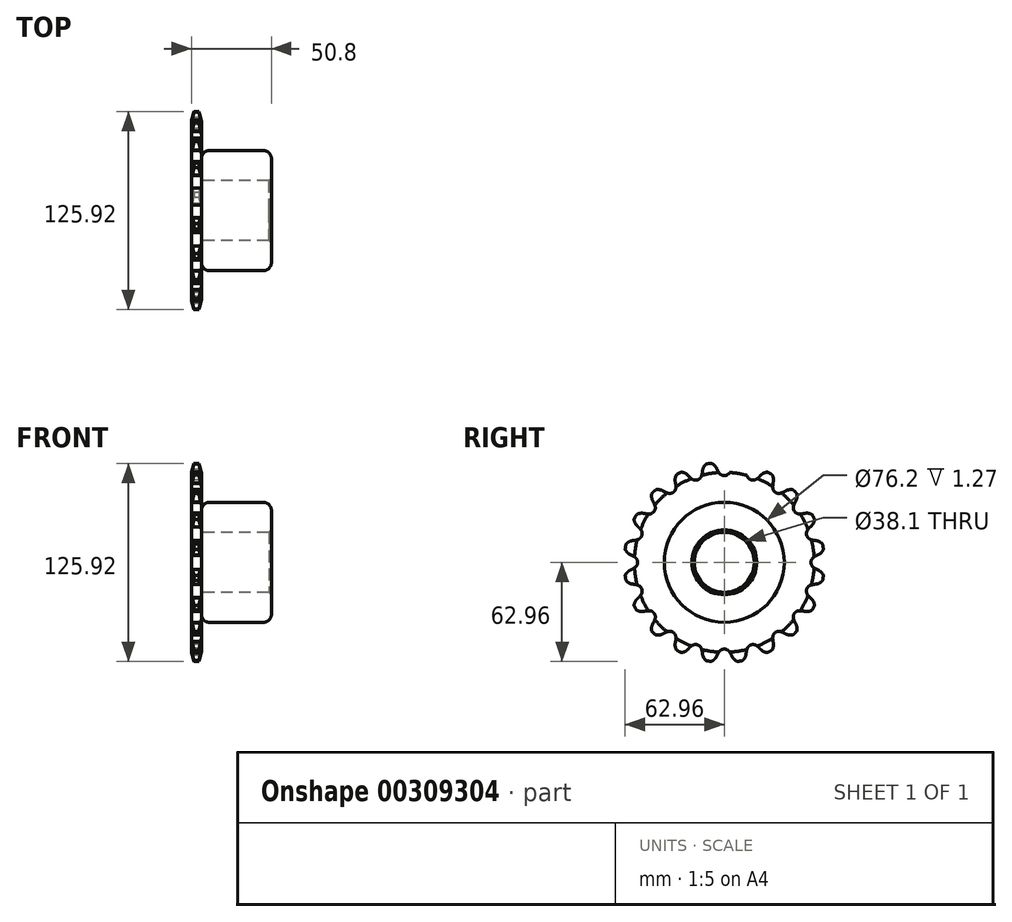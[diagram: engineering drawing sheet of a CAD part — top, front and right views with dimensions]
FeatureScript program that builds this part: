
annotation { "Feature Type Name" : "Feature", "Feature Type Description" : "" }
export const myFeature = defineFeature(function(context is Context, id is Id, definition is map)
    precondition{}
    {
        {
            var Q0;
            Q0=qCreatedBy(makeId("Top.planeOp"),FACE);
            var sketch = newSketch(context, id + "F0", { "sketchPlane" : qUnion([Q0])});
            skLineSegment(sketch, "E0", {"start": v(0, 0) * mm, "end": v(76.2, 0) * mm, "construction": true});
            skLineSegment(sketch, "E1.bottom", {"start": v(0, 19.05) * mm, "end": v(6.35, 19.05) * mm});
            skLineSegment(sketch, "E1.top", {"start": v(0, 63.5) * mm, "end": v(6.35, 63.5) * mm});
            skLineSegment(sketch, "E1.left", {"start": v(0, 19.05) * mm, "end": v(0, 63.5) * mm});
            skLineSegment(sketch, "E1.right", {"start": v(6.35, 19.05) * mm, "end": v(6.35, 63.5) * mm});
            skLineSegment(sketch, "E2.bottom", {"start": v(0, 19.05) * mm, "end": v(50.8, 19.05) * mm});
            skLineSegment(sketch, "E2.top", {"start": v(0, 38.1) * mm, "end": v(50.8, 38.1) * mm});
            skLineSegment(sketch, "E2.left", {"start": v(0, 19.05) * mm, "end": v(0, 38.1) * mm});
            skLineSegment(sketch, "E2.right", {"start": v(50.8, 19.05) * mm, "end": v(50.8, 38.1) * mm});
            skLineSegment(sketch, "E3.MirrorCS", {"start": v(0, -19.05) * mm, "end": v(6.35, -19.05) * mm});
            skLineSegment(sketch, "E4.MirrorCS", {"start": v(50.8, -19.05) * mm, "end": v(50.8, -38.1) * mm});
            skLineSegment(sketch, "E5.MirrorCS", {"start": v(0, -19.05) * mm, "end": v(0, -38.1) * mm});
            skLineSegment(sketch, "E6.MirrorCS", {"start": v(0, -19.05) * mm, "end": v(50.8, -19.05) * mm});
            skLineSegment(sketch, "E7.MirrorCS", {"start": v(0, -19.05) * mm, "end": v(0, -63.5) * mm});
            skLineSegment(sketch, "E8.MirrorCS", {"start": v(0, -38.1) * mm, "end": v(50.8, -38.1) * mm});
            skLineSegment(sketch, "E9.MirrorCS", {"start": v(0, -63.5) * mm, "end": v(6.35, -63.5) * mm});
            skLineSegment(sketch, "E10.MirrorCS", {"start": v(6.35, -19.05) * mm, "end": v(6.35, -63.5) * mm});
            skSolve(sketch);
        }
        {
            var Q0;
            {var subQ5=sQuery(id+"F0.wireOp",EDGE,"E2.right");Q0=makeQuery(id+"F0.imprint","IMPRINT",FACE,{"disambiguationData":[TD([[makeQuery(id+"F0.imprint","IMPRINT",EDGE,{"derivedFrom":subQ5}),1.0]])]});}
            var Q1;
            {var subQ5=sQuery(id+"F0.wireOp",EDGE,"E2.left");Q1=makeQuery(id+"F0.imprint","IMPRINT",FACE,{"disambiguationData":[TD([[makeQuery(id+"F0.imprint","IMPRINT",EDGE,{"derivedFrom":subQ5}),-1.0]])]});}
            var Q2;
            {var subQ0=sQuery(id+"F0.wireOp",EDGE,"E1.top");Q2=makeQuery(id+"F0.imprint","IMPRINT",FACE,{"disambiguationData":[TD([[makeQuery(id+"F0.imprint","IMPRINT",EDGE,{"derivedFrom":subQ0}),-1.0]])]});}
            var Q3;
            Q3=sQuery(id+"F0.wireOp",EDGE,"E0");
            revolve(context, id + "F1", {"entities" : qUnion([Q0, Q1, Q2]), "axis" : qUnion([Q3]), "revolveType" : RevolveType.FULL});
        }
        {
            var Q0;
            Q0=qCreatedBy(makeId("Right.planeOp"),FACE);
            var sketch = newSketch(context, id + "F2", { "sketchPlane" : qUnion([Q0])});
            skLineSegment(sketch, "E11", {"start": v(0, 0) * mm, "end": v(0, 59.03) * mm, "construction": true});
            skLineSegment(sketch, "E12", {"start": v(0, 59.03) * mm, "end": v(67.38, 59.03) * mm, "construction": true});
            skLineSegment(sketch, "E13", {"start": v(0, 59.03) * mm, "end": v(5, 63.04) * mm, "construction": true});
            skLineSegment(sketch, "E14", {"start": v(5, 63.04) * mm, "end": v(-4.46, 58.78) * mm, "construction": true});
            skLineSegment(sketch, "E15", {"start": v(-4.46, 58.78) * mm, "end": v(-7, 64.42) * mm, "construction": true});
            skLineSegment(sketch, "E16", {"start": v(0, 0) * mm, "end": v(-10.04, 63.42) * mm, "construction": true});
            skLineSegment(sketch, "E17", {"start": v(-10.04, 63.42) * mm, "end": v(-10.04, 63.42) * mm});
            skArc(sketch, "E18", {"start": v(-4.6, 59.03) * mm, "mid": v(-6.7, 62) * mm, "end": v(-10.04, 63.42) * mm});
            skArc(sketch, "E19", {"start": v(-10.04, 63.42) * mm, "mid": v(-14.96, 51.74) * mm, "end": v(-4.6, 59.03) * mm, "construction": true});
            skArc(sketch, "E20", {"start": v(-4.46, 58.78) * mm, "mid": v(-3.84, 57.62) * mm, "end": v(-3.1, 56.55) * mm});
            skArc(sketch, "E21", {"start": v(-3.1, 56.55) * mm, "mid": v(13.83, 68.45) * mm, "end": v(-4.46, 58.78) * mm, "construction": true});
            skLineSegment(sketch, "E22", {"start": v(-4.46, 58.78) * mm, "end": v(-4.46, 58.78) * mm});
            skArc(sketch, "E23", {"start": v(-3.1, 56.55) * mm, "mid": v(-1.71, 55.46) * mm, "end": v(0, 55.07) * mm});
            skLineSegment(sketch, "E24.MirrorCS", {"start": v(3.1, 56.55) * mm, "end": v(3.1, 56.55) * mm});
            skArc(sketch, "E25.MirrorCS", {"start": v(4.46, 58.78) * mm, "mid": v(3.84, 57.62) * mm, "end": v(3.1, 56.55) * mm});
            skArc(sketch, "E26.MirrorCS", {"start": v(4.6, 59.03) * mm, "mid": v(6.7, 62) * mm, "end": v(10.04, 63.42) * mm});
            skCircle(sketch, "E27", {"center": v(0, 0) * mm, "radius": 57.15 * mm});
            skLineSegment(sketch, "E28", {"start": v(4.6, 59.03) * mm, "end": v(4.46, 58.78) * mm});
            skLineSegment(sketch, "E29", {"start": v(-4.46, 58.78) * mm, "end": v(-4.6, 59.03) * mm});
            skLineSegment(sketch, "E30", {"start": v(0, 55.07) * mm, "end": v(0, 55.07) * mm});
            skArc(sketch, "E31", {"start": v(3.1, 56.55) * mm, "mid": v(1.71, 55.46) * mm, "end": v(0, 55.07) * mm});
            skArc(sketch, "E32.1.0", {"start": v(-14.54, 54.74) * mm, "mid": v(-15.5, 53.27) * mm, "end": v(-17.02, 52.37) * mm});
            skArc(sketch, "E32.1.1", {"start": v(-13.93, 57.28) * mm, "mid": v(-14.15, 55.99) * mm, "end": v(-14.54, 54.74) * mm});
            skLineSegment(sketch, "E32.1.2", {"start": v(-13.87, 57.56) * mm, "end": v(-13.93, 57.28) * mm});
            skArc(sketch, "E32.1.3", {"start": v(-13.87, 57.56) * mm, "mid": v(-12.8, 61.04) * mm, "end": v(-10.04, 63.42) * mm});
            skArc(sketch, "E32.1.4", {"start": v(-20.41, 52.83) * mm, "mid": v(-18.77, 52.21) * mm, "end": v(-17.02, 52.37) * mm});
            skArc(sketch, "E32.1.5", {"start": v(-22.4, 54.53) * mm, "mid": v(-21.46, 53.61) * mm, "end": v(-20.41, 52.83) * mm});
            skArc(sketch, "E32.1.6", {"start": v(-22.61, 54.72) * mm, "mid": v(-25.52, 56.9) * mm, "end": v(-29.15, 57.2) * mm});
            skLineSegment(sketch, "E32.1.7", {"start": v(-22.4, 54.53) * mm, "end": v(-22.61, 54.72) * mm});
            skArc(sketch, "E32.2.0", {"start": v(-30.74, 47.57) * mm, "mid": v(-31.21, 45.87) * mm, "end": v(-32.37, 44.55) * mm});
            skArc(sketch, "E32.2.1", {"start": v(-30.94, 50.17) * mm, "mid": v(-30.76, 48.88) * mm, "end": v(-30.74, 47.57) * mm});
            skLineSegment(sketch, "E32.2.2", {"start": v(-30.98, 50.46) * mm, "end": v(-30.94, 50.17) * mm});
            skArc(sketch, "E32.2.3", {"start": v(-30.98, 50.46) * mm, "mid": v(-31.03, 54.1) * mm, "end": v(-29.15, 57.2) * mm});
            skArc(sketch, "E32.2.4", {"start": v(-35.74, 43.93) * mm, "mid": v(-33.98, 43.86) * mm, "end": v(-32.37, 44.55) * mm});
            skArc(sketch, "E32.2.5", {"start": v(-38.16, 44.93) * mm, "mid": v(-36.98, 44.36) * mm, "end": v(-35.74, 43.93) * mm});
            skArc(sketch, "E32.2.6", {"start": v(-38.41, 45.05) * mm, "mid": v(-41.86, 46.23) * mm, "end": v(-45.4, 45.4) * mm});
            skLineSegment(sketch, "E32.2.7", {"start": v(-38.16, 44.93) * mm, "end": v(-38.41, 45.05) * mm});
            skArc(sketch, "E33.3.3.0", {"start": v(-43.93, 35.74) * mm, "mid": v(-43.86, 33.98) * mm, "end": v(-44.55, 32.37) * mm});
            skArc(sketch, "E33.4.3.0", {"start": v(-44.93, 38.16) * mm, "mid": v(-44.36, 36.98) * mm, "end": v(-43.93, 35.74) * mm});
            skLineSegment(sketch, "E33.8.3.0", {"start": v(-45.05, 38.41) * mm, "end": v(-44.93, 38.16) * mm});
            skArc(sketch, "E33.11.3.0", {"start": v(-45.05, 38.41) * mm, "mid": v(-46.23, 41.86) * mm, "end": v(-45.4, 45.4) * mm});
            skArc(sketch, "E33.15.3.0", {"start": v(-47.57, 30.74) * mm, "mid": v(-45.87, 31.21) * mm, "end": v(-44.55, 32.37) * mm});
            skArc(sketch, "E33.19.3.0", {"start": v(-50.17, 30.94) * mm, "mid": v(-48.88, 30.76) * mm, "end": v(-47.57, 30.74) * mm});
            skArc(sketch, "E33.23.3.0", {"start": v(-50.46, 30.98) * mm, "mid": v(-54.1, 31.03) * mm, "end": v(-57.2, 29.15) * mm});
            skLineSegment(sketch, "E33.27.3.0", {"start": v(-50.17, 30.94) * mm, "end": v(-50.46, 30.98) * mm});
            skArc(sketch, "E33.3.4.0", {"start": v(-52.83, 20.41) * mm, "mid": v(-52.21, 18.77) * mm, "end": v(-52.37, 17.02) * mm});
            skArc(sketch, "E33.4.4.0", {"start": v(-54.53, 22.4) * mm, "mid": v(-53.61, 21.46) * mm, "end": v(-52.83, 20.41) * mm});
            skLineSegment(sketch, "E33.8.4.0", {"start": v(-54.72, 22.61) * mm, "end": v(-54.53, 22.4) * mm});
            skArc(sketch, "E33.11.4.0", {"start": v(-54.72, 22.61) * mm, "mid": v(-56.9, 25.52) * mm, "end": v(-57.2, 29.15) * mm});
            skArc(sketch, "E33.15.4.0", {"start": v(-54.74, 14.54) * mm, "mid": v(-53.27, 15.5) * mm, "end": v(-52.37, 17.02) * mm});
            skArc(sketch, "E33.19.4.0", {"start": v(-57.28, 13.93) * mm, "mid": v(-55.99, 14.15) * mm, "end": v(-54.74, 14.54) * mm});
            skArc(sketch, "E33.23.4.0", {"start": v(-57.56, 13.87) * mm, "mid": v(-61.04, 12.8) * mm, "end": v(-63.42, 10.04) * mm});
            skLineSegment(sketch, "E33.27.4.0", {"start": v(-57.28, 13.93) * mm, "end": v(-57.56, 13.87) * mm});
            skArc(sketch, "E33.3.5.0", {"start": v(-56.55, 3.1) * mm, "mid": v(-55.46, 1.71) * mm, "end": v(-55.07, 0) * mm});
            skArc(sketch, "E33.4.5.0", {"start": v(-58.78, 4.46) * mm, "mid": v(-57.62, 3.84) * mm, "end": v(-56.55, 3.1) * mm});
            skLineSegment(sketch, "E33.8.5.0", {"start": v(-59.03, 4.6) * mm, "end": v(-58.78, 4.46) * mm});
            skArc(sketch, "E33.11.5.0", {"start": v(-59.03, 4.6) * mm, "mid": v(-62, 6.7) * mm, "end": v(-63.42, 10.04) * mm});
            skArc(sketch, "E33.15.5.0", {"start": v(-56.55, -3.1) * mm, "mid": v(-55.46, -1.71) * mm, "end": v(-55.07, 0) * mm});
            skArc(sketch, "E33.19.5.0", {"start": v(-58.78, -4.46) * mm, "mid": v(-57.62, -3.84) * mm, "end": v(-56.55, -3.1) * mm});
            skArc(sketch, "E33.23.5.0", {"start": v(-59.03, -4.6) * mm, "mid": v(-62, -6.7) * mm, "end": v(-63.42, -10.04) * mm});
            skLineSegment(sketch, "E33.27.5.0", {"start": v(-58.78, -4.46) * mm, "end": v(-59.03, -4.6) * mm});
            skArc(sketch, "E33.3.6.0", {"start": v(-54.74, -14.54) * mm, "mid": v(-53.27, -15.5) * mm, "end": v(-52.37, -17.02) * mm});
            skArc(sketch, "E33.4.6.0", {"start": v(-57.28, -13.93) * mm, "mid": v(-55.99, -14.15) * mm, "end": v(-54.74, -14.54) * mm});
            skLineSegment(sketch, "E33.8.6.0", {"start": v(-57.56, -13.87) * mm, "end": v(-57.28, -13.93) * mm});
            skArc(sketch, "E33.11.6.0", {"start": v(-57.56, -13.87) * mm, "mid": v(-61.04, -12.8) * mm, "end": v(-63.42, -10.04) * mm});
            skArc(sketch, "E33.15.6.0", {"start": v(-52.83, -20.41) * mm, "mid": v(-52.21, -18.77) * mm, "end": v(-52.37, -17.02) * mm});
            skArc(sketch, "E33.19.6.0", {"start": v(-54.53, -22.4) * mm, "mid": v(-53.61, -21.46) * mm, "end": v(-52.83, -20.41) * mm});
            skArc(sketch, "E33.23.6.0", {"start": v(-54.72, -22.61) * mm, "mid": v(-56.9, -25.52) * mm, "end": v(-57.2, -29.15) * mm});
            skLineSegment(sketch, "E33.27.6.0", {"start": v(-54.53, -22.4) * mm, "end": v(-54.72, -22.61) * mm});
            skArc(sketch, "E33.3.7.0", {"start": v(-47.57, -30.74) * mm, "mid": v(-45.87, -31.21) * mm, "end": v(-44.55, -32.37) * mm});
            skArc(sketch, "E33.4.7.0", {"start": v(-50.17, -30.94) * mm, "mid": v(-48.88, -30.76) * mm, "end": v(-47.57, -30.74) * mm});
            skLineSegment(sketch, "E33.8.7.0", {"start": v(-50.46, -30.98) * mm, "end": v(-50.17, -30.94) * mm});
            skArc(sketch, "E33.11.7.0", {"start": v(-50.46, -30.98) * mm, "mid": v(-54.1, -31.03) * mm, "end": v(-57.2, -29.15) * mm});
            skArc(sketch, "E33.15.7.0", {"start": v(-43.93, -35.74) * mm, "mid": v(-43.86, -33.98) * mm, "end": v(-44.55, -32.37) * mm});
            skArc(sketch, "E33.19.7.0", {"start": v(-44.93, -38.16) * mm, "mid": v(-44.36, -36.98) * mm, "end": v(-43.93, -35.74) * mm});
            skArc(sketch, "E33.23.7.0", {"start": v(-45.05, -38.41) * mm, "mid": v(-46.23, -41.86) * mm, "end": v(-45.4, -45.4) * mm});
            skLineSegment(sketch, "E33.27.7.0", {"start": v(-44.93, -38.16) * mm, "end": v(-45.05, -38.41) * mm});
            skArc(sketch, "E33.3.8.0", {"start": v(-35.74, -43.93) * mm, "mid": v(-33.98, -43.86) * mm, "end": v(-32.37, -44.55) * mm});
            skArc(sketch, "E33.4.8.0", {"start": v(-38.16, -44.93) * mm, "mid": v(-36.98, -44.36) * mm, "end": v(-35.74, -43.93) * mm});
            skLineSegment(sketch, "E33.8.8.0", {"start": v(-38.41, -45.05) * mm, "end": v(-38.16, -44.93) * mm});
            skArc(sketch, "E33.11.8.0", {"start": v(-38.41, -45.05) * mm, "mid": v(-41.86, -46.23) * mm, "end": v(-45.4, -45.4) * mm});
            skArc(sketch, "E33.15.8.0", {"start": v(-30.74, -47.57) * mm, "mid": v(-31.21, -45.87) * mm, "end": v(-32.37, -44.55) * mm});
            skArc(sketch, "E33.19.8.0", {"start": v(-30.94, -50.17) * mm, "mid": v(-30.76, -48.88) * mm, "end": v(-30.74, -47.57) * mm});
            skArc(sketch, "E33.23.8.0", {"start": v(-30.98, -50.46) * mm, "mid": v(-31.03, -54.1) * mm, "end": v(-29.15, -57.2) * mm});
            skLineSegment(sketch, "E33.27.8.0", {"start": v(-30.94, -50.17) * mm, "end": v(-30.98, -50.46) * mm});
            skArc(sketch, "E33.3.9.0", {"start": v(-20.41, -52.83) * mm, "mid": v(-18.77, -52.21) * mm, "end": v(-17.02, -52.37) * mm});
            skArc(sketch, "E33.4.9.0", {"start": v(-22.4, -54.53) * mm, "mid": v(-21.46, -53.61) * mm, "end": v(-20.41, -52.83) * mm});
            skLineSegment(sketch, "E33.8.9.0", {"start": v(-22.61, -54.72) * mm, "end": v(-22.4, -54.53) * mm});
            skArc(sketch, "E33.11.9.0", {"start": v(-22.61, -54.72) * mm, "mid": v(-25.52, -56.9) * mm, "end": v(-29.15, -57.2) * mm});
            skArc(sketch, "E33.15.9.0", {"start": v(-14.54, -54.74) * mm, "mid": v(-15.5, -53.27) * mm, "end": v(-17.02, -52.37) * mm});
            skArc(sketch, "E33.19.9.0", {"start": v(-13.93, -57.28) * mm, "mid": v(-14.15, -55.99) * mm, "end": v(-14.54, -54.74) * mm});
            skArc(sketch, "E33.23.9.0", {"start": v(-13.87, -57.56) * mm, "mid": v(-12.8, -61.04) * mm, "end": v(-10.04, -63.42) * mm});
            skLineSegment(sketch, "E33.27.9.0", {"start": v(-13.93, -57.28) * mm, "end": v(-13.87, -57.56) * mm});
            skArc(sketch, "E33.3.10.0", {"start": v(-3.1, -56.55) * mm, "mid": v(-1.71, -55.46) * mm, "end": v(0, -55.07) * mm});
            skArc(sketch, "E33.4.10.0", {"start": v(-4.46, -58.78) * mm, "mid": v(-3.84, -57.62) * mm, "end": v(-3.1, -56.55) * mm});
            skLineSegment(sketch, "E33.8.10.0", {"start": v(-4.6, -59.03) * mm, "end": v(-4.46, -58.78) * mm});
            skArc(sketch, "E33.11.10.0", {"start": v(-4.6, -59.03) * mm, "mid": v(-6.7, -62) * mm, "end": v(-10.04, -63.42) * mm});
            skArc(sketch, "E33.15.10.0", {"start": v(3.1, -56.55) * mm, "mid": v(1.71, -55.46) * mm, "end": v(0, -55.07) * mm});
            skArc(sketch, "E33.19.10.0", {"start": v(4.46, -58.78) * mm, "mid": v(3.84, -57.62) * mm, "end": v(3.1, -56.55) * mm});
            skArc(sketch, "E33.23.10.0", {"start": v(4.6, -59.03) * mm, "mid": v(6.7, -62) * mm, "end": v(10.04, -63.42) * mm});
            skLineSegment(sketch, "E33.27.10.0", {"start": v(4.46, -58.78) * mm, "end": v(4.6, -59.03) * mm});
            skArc(sketch, "E33.3.11.0", {"start": v(14.54, -54.74) * mm, "mid": v(15.5, -53.27) * mm, "end": v(17.02, -52.37) * mm});
            skArc(sketch, "E33.4.11.0", {"start": v(13.93, -57.28) * mm, "mid": v(14.15, -55.99) * mm, "end": v(14.54, -54.74) * mm});
            skLineSegment(sketch, "E33.8.11.0", {"start": v(13.87, -57.56) * mm, "end": v(13.93, -57.28) * mm});
            skArc(sketch, "E33.11.11.0", {"start": v(13.87, -57.56) * mm, "mid": v(12.8, -61.04) * mm, "end": v(10.04, -63.42) * mm});
            skArc(sketch, "E33.15.11.0", {"start": v(20.41, -52.83) * mm, "mid": v(18.77, -52.21) * mm, "end": v(17.02, -52.37) * mm});
            skArc(sketch, "E33.19.11.0", {"start": v(22.4, -54.53) * mm, "mid": v(21.46, -53.61) * mm, "end": v(20.41, -52.83) * mm});
            skArc(sketch, "E33.23.11.0", {"start": v(22.61, -54.72) * mm, "mid": v(25.52, -56.9) * mm, "end": v(29.15, -57.2) * mm});
            skLineSegment(sketch, "E33.27.11.0", {"start": v(22.4, -54.53) * mm, "end": v(22.61, -54.72) * mm});
            skArc(sketch, "E33.3.12.0", {"start": v(30.74, -47.57) * mm, "mid": v(31.21, -45.87) * mm, "end": v(32.37, -44.55) * mm});
            skArc(sketch, "E33.4.12.0", {"start": v(30.94, -50.17) * mm, "mid": v(30.76, -48.88) * mm, "end": v(30.74, -47.57) * mm});
            skLineSegment(sketch, "E33.8.12.0", {"start": v(30.98, -50.46) * mm, "end": v(30.94, -50.17) * mm});
            skArc(sketch, "E33.11.12.0", {"start": v(30.98, -50.46) * mm, "mid": v(31.03, -54.1) * mm, "end": v(29.15, -57.2) * mm});
            skArc(sketch, "E33.15.12.0", {"start": v(35.74, -43.93) * mm, "mid": v(33.98, -43.86) * mm, "end": v(32.37, -44.55) * mm});
            skArc(sketch, "E33.19.12.0", {"start": v(38.16, -44.93) * mm, "mid": v(36.98, -44.36) * mm, "end": v(35.74, -43.93) * mm});
            skArc(sketch, "E33.23.12.0", {"start": v(38.41, -45.05) * mm, "mid": v(41.86, -46.23) * mm, "end": v(45.4, -45.4) * mm});
            skLineSegment(sketch, "E33.27.12.0", {"start": v(38.16, -44.93) * mm, "end": v(38.41, -45.05) * mm});
            skArc(sketch, "E33.3.13.0", {"start": v(43.93, -35.74) * mm, "mid": v(43.86, -33.98) * mm, "end": v(44.55, -32.37) * mm});
            skArc(sketch, "E33.4.13.0", {"start": v(44.93, -38.16) * mm, "mid": v(44.36, -36.98) * mm, "end": v(43.93, -35.74) * mm});
            skLineSegment(sketch, "E33.8.13.0", {"start": v(45.05, -38.41) * mm, "end": v(44.93, -38.16) * mm});
            skArc(sketch, "E33.11.13.0", {"start": v(45.05, -38.41) * mm, "mid": v(46.23, -41.86) * mm, "end": v(45.4, -45.4) * mm});
            skArc(sketch, "E33.15.13.0", {"start": v(47.57, -30.74) * mm, "mid": v(45.87, -31.21) * mm, "end": v(44.55, -32.37) * mm});
            skArc(sketch, "E33.19.13.0", {"start": v(50.17, -30.94) * mm, "mid": v(48.88, -30.76) * mm, "end": v(47.57, -30.74) * mm});
            skArc(sketch, "E33.23.13.0", {"start": v(50.46, -30.98) * mm, "mid": v(54.1, -31.03) * mm, "end": v(57.2, -29.15) * mm});
            skLineSegment(sketch, "E33.27.13.0", {"start": v(50.17, -30.94) * mm, "end": v(50.46, -30.98) * mm});
            skArc(sketch, "E33.3.14.0", {"start": v(52.83, -20.41) * mm, "mid": v(52.21, -18.77) * mm, "end": v(52.37, -17.02) * mm});
            skArc(sketch, "E33.4.14.0", {"start": v(54.53, -22.4) * mm, "mid": v(53.61, -21.46) * mm, "end": v(52.83, -20.41) * mm});
            skLineSegment(sketch, "E33.8.14.0", {"start": v(54.72, -22.61) * mm, "end": v(54.53, -22.4) * mm});
            skArc(sketch, "E33.11.14.0", {"start": v(54.72, -22.61) * mm, "mid": v(56.9, -25.52) * mm, "end": v(57.2, -29.15) * mm});
            skArc(sketch, "E33.15.14.0", {"start": v(54.74, -14.54) * mm, "mid": v(53.27, -15.5) * mm, "end": v(52.37, -17.02) * mm});
            skArc(sketch, "E33.19.14.0", {"start": v(57.28, -13.93) * mm, "mid": v(55.99, -14.15) * mm, "end": v(54.74, -14.54) * mm});
            skArc(sketch, "E33.23.14.0", {"start": v(57.56, -13.87) * mm, "mid": v(61.04, -12.8) * mm, "end": v(63.42, -10.04) * mm});
            skLineSegment(sketch, "E33.27.14.0", {"start": v(57.28, -13.93) * mm, "end": v(57.56, -13.87) * mm});
            skArc(sketch, "E33.3.15.0", {"start": v(56.55, -3.1) * mm, "mid": v(55.46, -1.71) * mm, "end": v(55.07, 0) * mm});
            skArc(sketch, "E33.4.15.0", {"start": v(58.78, -4.46) * mm, "mid": v(57.62, -3.84) * mm, "end": v(56.55, -3.1) * mm});
            skLineSegment(sketch, "E33.8.15.0", {"start": v(59.03, -4.6) * mm, "end": v(58.78, -4.46) * mm});
            skArc(sketch, "E33.11.15.0", {"start": v(59.03, -4.6) * mm, "mid": v(62, -6.7) * mm, "end": v(63.42, -10.04) * mm});
            skArc(sketch, "E33.15.15.0", {"start": v(56.55, 3.1) * mm, "mid": v(55.46, 1.71) * mm, "end": v(55.07, 0) * mm});
            skArc(sketch, "E33.19.15.0", {"start": v(58.78, 4.46) * mm, "mid": v(57.62, 3.84) * mm, "end": v(56.55, 3.1) * mm});
            skArc(sketch, "E33.23.15.0", {"start": v(59.03, 4.6) * mm, "mid": v(62, 6.7) * mm, "end": v(63.42, 10.04) * mm});
            skLineSegment(sketch, "E33.27.15.0", {"start": v(58.78, 4.46) * mm, "end": v(59.03, 4.6) * mm});
            skArc(sketch, "E33.3.16.0", {"start": v(54.74, 14.54) * mm, "mid": v(53.27, 15.5) * mm, "end": v(52.37, 17.02) * mm});
            skArc(sketch, "E33.4.16.0", {"start": v(57.28, 13.93) * mm, "mid": v(55.99, 14.15) * mm, "end": v(54.74, 14.54) * mm});
            skLineSegment(sketch, "E33.8.16.0", {"start": v(57.56, 13.87) * mm, "end": v(57.28, 13.93) * mm});
            skArc(sketch, "E33.11.16.0", {"start": v(57.56, 13.87) * mm, "mid": v(61.04, 12.8) * mm, "end": v(63.42, 10.04) * mm});
            skArc(sketch, "E33.15.16.0", {"start": v(52.83, 20.41) * mm, "mid": v(52.21, 18.77) * mm, "end": v(52.37, 17.02) * mm});
            skArc(sketch, "E33.19.16.0", {"start": v(54.53, 22.4) * mm, "mid": v(53.61, 21.46) * mm, "end": v(52.83, 20.41) * mm});
            skArc(sketch, "E33.23.16.0", {"start": v(54.72, 22.61) * mm, "mid": v(56.9, 25.52) * mm, "end": v(57.2, 29.15) * mm});
            skLineSegment(sketch, "E33.27.16.0", {"start": v(54.53, 22.4) * mm, "end": v(54.72, 22.61) * mm});
            skArc(sketch, "E33.3.17.0", {"start": v(47.57, 30.74) * mm, "mid": v(45.87, 31.21) * mm, "end": v(44.55, 32.37) * mm});
            skArc(sketch, "E33.4.17.0", {"start": v(50.17, 30.94) * mm, "mid": v(48.88, 30.76) * mm, "end": v(47.57, 30.74) * mm});
            skLineSegment(sketch, "E33.8.17.0", {"start": v(50.46, 30.98) * mm, "end": v(50.17, 30.94) * mm});
            skArc(sketch, "E33.11.17.0", {"start": v(50.46, 30.98) * mm, "mid": v(54.1, 31.03) * mm, "end": v(57.2, 29.15) * mm});
            skArc(sketch, "E33.15.17.0", {"start": v(43.93, 35.74) * mm, "mid": v(43.86, 33.98) * mm, "end": v(44.55, 32.37) * mm});
            skArc(sketch, "E33.19.17.0", {"start": v(44.93, 38.16) * mm, "mid": v(44.36, 36.98) * mm, "end": v(43.93, 35.74) * mm});
            skArc(sketch, "E33.23.17.0", {"start": v(45.05, 38.41) * mm, "mid": v(46.23, 41.86) * mm, "end": v(45.4, 45.4) * mm});
            skLineSegment(sketch, "E33.27.17.0", {"start": v(44.93, 38.16) * mm, "end": v(45.05, 38.41) * mm});
            skArc(sketch, "E33.3.18.0", {"start": v(35.74, 43.93) * mm, "mid": v(33.98, 43.86) * mm, "end": v(32.37, 44.55) * mm});
            skArc(sketch, "E33.4.18.0", {"start": v(38.16, 44.93) * mm, "mid": v(36.98, 44.36) * mm, "end": v(35.74, 43.93) * mm});
            skLineSegment(sketch, "E33.8.18.0", {"start": v(38.41, 45.05) * mm, "end": v(38.16, 44.93) * mm});
            skArc(sketch, "E33.11.18.0", {"start": v(38.41, 45.05) * mm, "mid": v(41.86, 46.23) * mm, "end": v(45.4, 45.4) * mm});
            skArc(sketch, "E33.15.18.0", {"start": v(30.74, 47.57) * mm, "mid": v(31.21, 45.87) * mm, "end": v(32.37, 44.55) * mm});
            skArc(sketch, "E33.19.18.0", {"start": v(30.94, 50.17) * mm, "mid": v(30.76, 48.88) * mm, "end": v(30.74, 47.57) * mm});
            skArc(sketch, "E33.23.18.0", {"start": v(30.98, 50.46) * mm, "mid": v(31.03, 54.1) * mm, "end": v(29.15, 57.2) * mm});
            skLineSegment(sketch, "E33.27.18.0", {"start": v(30.94, 50.17) * mm, "end": v(30.98, 50.46) * mm});
            skArc(sketch, "E33.3.19.0", {"start": v(20.41, 52.83) * mm, "mid": v(18.77, 52.21) * mm, "end": v(17.02, 52.37) * mm});
            skArc(sketch, "E33.4.19.0", {"start": v(22.4, 54.53) * mm, "mid": v(21.46, 53.61) * mm, "end": v(20.41, 52.83) * mm});
            skLineSegment(sketch, "E33.8.19.0", {"start": v(22.61, 54.72) * mm, "end": v(22.4, 54.53) * mm});
            skArc(sketch, "E33.11.19.0", {"start": v(22.61, 54.72) * mm, "mid": v(25.52, 56.9) * mm, "end": v(29.15, 57.2) * mm});
            skArc(sketch, "E33.15.19.0", {"start": v(14.54, 54.74) * mm, "mid": v(15.5, 53.27) * mm, "end": v(17.02, 52.37) * mm});
            skArc(sketch, "E33.19.19.0", {"start": v(13.93, 57.28) * mm, "mid": v(14.15, 55.99) * mm, "end": v(14.54, 54.74) * mm});
            skArc(sketch, "E33.23.19.0", {"start": v(13.87, 57.56) * mm, "mid": v(12.8, 61.04) * mm, "end": v(10.04, 63.42) * mm});
            skLineSegment(sketch, "E33.27.19.0", {"start": v(13.93, 57.28) * mm, "end": v(13.87, 57.56) * mm});
            skSolve(sketch);
        }
        {
            var Q0;
            Q0=makeQuery(id+"F1.opRevolve","SWEPT_FACE",FACE,{"disambiguationData":[OSD([sQuery(id+"F0.wireOp",EDGE,"E1.top")])]});
            chamfer(context, id + "F3", {"entities" : qUnion([Q0]), "chamferType" : ChamferType.TWO_OFFSETS, "width1" : 6.35 * mm, "oppositeDirection" : false, "width2" : 1.59 * mm, "tangentPropagation" : true});
        }
        {
            var Q0;
            Q0=makeQuery(id+"F1.opRevolve","SWEPT_EDGE",EDGE,{"disambiguationData":[OSD([sQuery(id+"F0.wireOp",EDGE,"E1.right"),sQuery(id+"F0.wireOp",EDGE,"E2.top")])]});
            var Q1;
            Q1=makeQuery(id+"F1.opRevolve","SWEPT_EDGE",EDGE,{"disambiguationData":[OSD([sQuery(id+"F0.wireOp",EDGE,"E2.top"),sQuery(id+"F0.wireOp",EDGE,"E2.right")])]});
            fillet(context, id + "F4", {"entities" : qUnion([Q0, Q1]), "radius" : 5.08 * mm, "tangentPropagation" : true, "allowEdgeOverflow" : false});
        }
        {
            var Q0;
            Q0=makeQuery(id+"F1.opRevolve","SWEPT_EDGE",EDGE,{"disambiguationData":[OSD([sQuery(id+"F0.wireOp",EDGE,"E2.bottom"),sQuery(id+"F0.wireOp",EDGE,"E2.right")])]});
            var Q1;
            Q1=makeQuery(id+"F1.opRevolve","SWEPT_EDGE",EDGE,{"disambiguationData":[OSD([sQuery(id+"F0.wireOp",EDGE,"E2.bottom"),sQuery(id+"F0.wireOp",EDGE,"E2.left")])]});
            chamfer(context, id + "F5", {"entities" : qUnion([Q0, Q1]), "width" : 1.59 * mm, "tangentPropagation" : true});
        }
        {
            var Q0;
            Q0=makeQuery(id+"F2.imprint","IMPRINT",FACE,{"disambiguationData":[TD([[makeQuery(id+"F2.imprint","IMPRINT",EDGE,{"derivedFrom":sQuery(id+"F2.wireOp",EDGE,"E18")}),1.0]])]});
            var Q1;
            Q1=makeQuery(id+"F2.imprint","IMPRINT",FACE,{"disambiguationData":[TD([[makeQuery(id+"F2.imprint","IMPRINT",EDGE,{"derivedFrom":sQuery(id+"F2.wireOp",EDGE,"E26.MirrorCS")}),-1.0]])]});
            var Q2;
            Q2=makeQuery(id+"F2.imprint","IMPRINT",FACE,{"disambiguationData":[TD([[makeQuery(id+"F2.imprint","IMPRINT",EDGE,{"derivedFrom":sQuery(id+"F2.wireOp",EDGE,"E33.23.15.0")}),1.0]])]});
            var Q3;
            Q3=makeQuery(id+"F2.imprint","IMPRINT",FACE,{"disambiguationData":[TD([[makeQuery(id+"F2.imprint","IMPRINT",EDGE,{"derivedFrom":sQuery(id+"F2.wireOp",EDGE,"E33.23.16.0")}),1.0]])]});
            var Q4;
            Q4=makeQuery(id+"F2.imprint","IMPRINT",FACE,{"disambiguationData":[TD([[makeQuery(id+"F2.imprint","IMPRINT",EDGE,{"derivedFrom":sQuery(id+"F2.wireOp",EDGE,"E33.23.17.0")}),1.0]])]});
            var Q5;
            Q5=makeQuery(id+"F2.imprint","IMPRINT",FACE,{"disambiguationData":[TD([[makeQuery(id+"F2.imprint","IMPRINT",EDGE,{"derivedFrom":sQuery(id+"F2.wireOp",EDGE,"E33.23.18.0")}),1.0]])]});
            var Q6;
            Q6=makeQuery(id+"F2.imprint","IMPRINT",FACE,{"disambiguationData":[TD([[makeQuery(id+"F2.imprint","IMPRINT",EDGE,{"derivedFrom":sQuery(id+"F2.wireOp",EDGE,"E32.1.6")}),1.0]])]});
            var Q7;
            Q7=makeQuery(id+"F2.imprint","IMPRINT",FACE,{"disambiguationData":[TD([[makeQuery(id+"F2.imprint","IMPRINT",EDGE,{"derivedFrom":sQuery(id+"F2.wireOp",EDGE,"E32.2.6")}),1.0]])]});
            var Q8;
            Q8=makeQuery(id+"F2.imprint","IMPRINT",FACE,{"disambiguationData":[TD([[makeQuery(id+"F2.imprint","IMPRINT",EDGE,{"derivedFrom":sQuery(id+"F2.wireOp",EDGE,"E33.23.3.0")}),1.0]])]});
            var Q9;
            Q9=makeQuery(id+"F2.imprint","IMPRINT",FACE,{"disambiguationData":[TD([[makeQuery(id+"F2.imprint","IMPRINT",EDGE,{"derivedFrom":sQuery(id+"F2.wireOp",EDGE,"E33.23.4.0")}),1.0]])]});
            var Q10;
            Q10=makeQuery(id+"F2.imprint","IMPRINT",FACE,{"disambiguationData":[TD([[makeQuery(id+"F2.imprint","IMPRINT",EDGE,{"derivedFrom":sQuery(id+"F2.wireOp",EDGE,"E33.23.5.0")}),1.0]])]});
            var Q11;
            Q11=makeQuery(id+"F2.imprint","IMPRINT",FACE,{"disambiguationData":[TD([[makeQuery(id+"F2.imprint","IMPRINT",EDGE,{"derivedFrom":sQuery(id+"F2.wireOp",EDGE,"E33.23.6.0")}),1.0]])]});
            var Q12;
            Q12=makeQuery(id+"F2.imprint","IMPRINT",FACE,{"disambiguationData":[TD([[makeQuery(id+"F2.imprint","IMPRINT",EDGE,{"derivedFrom":sQuery(id+"F2.wireOp",EDGE,"E33.23.7.0")}),1.0]])]});
            var Q13;
            Q13=makeQuery(id+"F2.imprint","IMPRINT",FACE,{"disambiguationData":[TD([[makeQuery(id+"F2.imprint","IMPRINT",EDGE,{"derivedFrom":sQuery(id+"F2.wireOp",EDGE,"E33.23.8.0")}),1.0]])]});
            var Q14;
            Q14=makeQuery(id+"F2.imprint","IMPRINT",FACE,{"disambiguationData":[TD([[makeQuery(id+"F2.imprint","IMPRINT",EDGE,{"derivedFrom":sQuery(id+"F2.wireOp",EDGE,"E33.23.9.0")}),1.0]])]});
            var Q15;
            Q15=makeQuery(id+"F2.imprint","IMPRINT",FACE,{"disambiguationData":[TD([[makeQuery(id+"F2.imprint","IMPRINT",EDGE,{"derivedFrom":sQuery(id+"F2.wireOp",EDGE,"E33.23.10.0")}),1.0]])]});
            var Q16;
            Q16=makeQuery(id+"F2.imprint","IMPRINT",FACE,{"disambiguationData":[TD([[makeQuery(id+"F2.imprint","IMPRINT",EDGE,{"derivedFrom":sQuery(id+"F2.wireOp",EDGE,"E33.23.11.0")}),1.0]])]});
            var Q17;
            Q17=makeQuery(id+"F2.imprint","IMPRINT",FACE,{"disambiguationData":[TD([[makeQuery(id+"F2.imprint","IMPRINT",EDGE,{"derivedFrom":sQuery(id+"F2.wireOp",EDGE,"E33.23.12.0")}),1.0]])]});
            var Q18;
            Q18=makeQuery(id+"F2.imprint","IMPRINT",FACE,{"disambiguationData":[TD([[makeQuery(id+"F2.imprint","IMPRINT",EDGE,{"derivedFrom":sQuery(id+"F2.wireOp",EDGE,"E33.23.13.0")}),1.0]])]});
            var Q19;
            Q19=makeQuery(id+"F2.imprint","IMPRINT",FACE,{"disambiguationData":[TD([[makeQuery(id+"F2.imprint","IMPRINT",EDGE,{"derivedFrom":sQuery(id+"F2.wireOp",EDGE,"E33.23.14.0")}),1.0]])]});
            var Q20;
            {var subQ47=sQuery(id+"F2.wireOp",EDGE,"E23");Q20=makeQuery(id+"F2.imprint","IMPRINT",FACE,{"disambiguationData":[TD([[makeQuery(id+"F2.imprint","IMPRINT",EDGE,{"derivedFrom":subQ47}),-1.0]])]});}
            extrude(context, id + "F6", {"entities" : qUnion([Q0, Q1, Q2, Q3, Q4, Q5, Q6, Q7, Q8, Q9, Q10, Q11, Q12, Q13, Q14, Q15, Q16, Q17, Q18, Q19, Q20]), "operationType" : NewBodyOperationType.INTERSECT, "endBound" : BoundingType.THROUGH_ALL, "depth" : 25.4 * mm});
        }
    });
